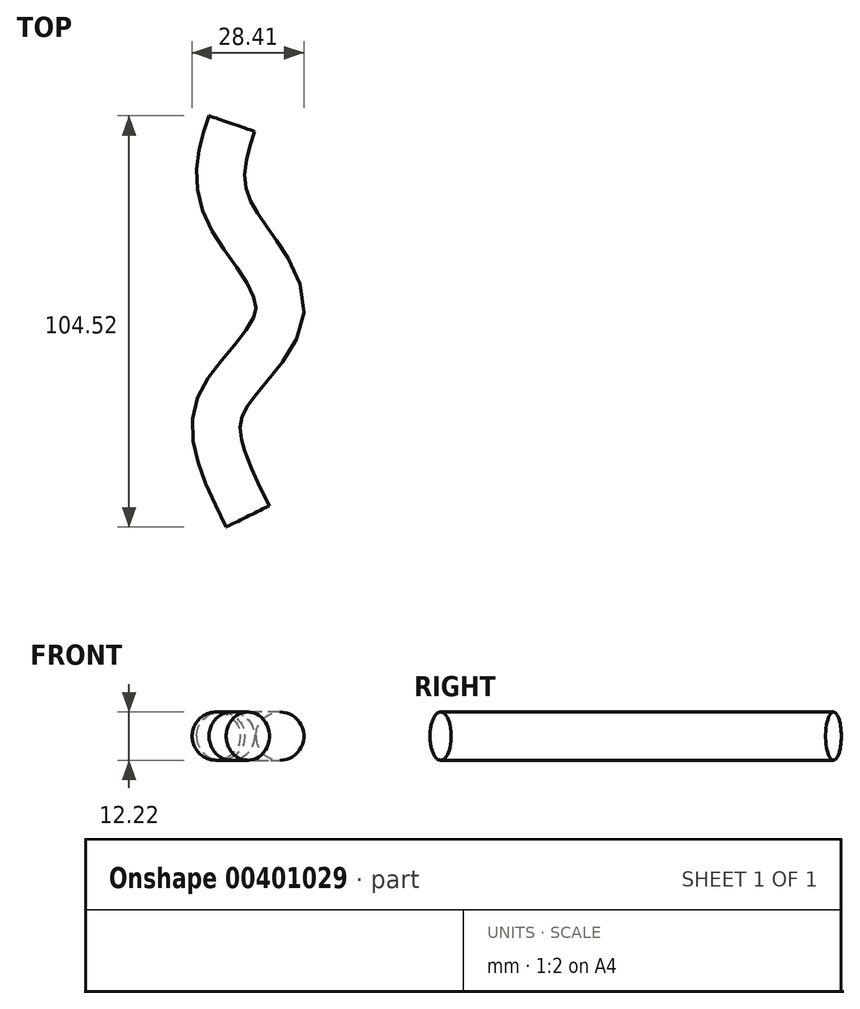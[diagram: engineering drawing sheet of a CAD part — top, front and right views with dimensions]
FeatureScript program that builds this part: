
annotation { "Feature Type Name" : "Feature", "Feature Type Description" : "" }
export const myFeature = defineFeature(function(context is Context, id is Id, definition is map)
    precondition{}
    {
        {
            var Q0;
            Q0=qCreatedBy(makeId("Top.planeOp"),FACE);
            var sketch = newSketch(context, id + "F0", { "sketchPlane" : qUnion([Q0])});
            skFitSpline(sketch, "E0", {"points": [v(-116.4, -34.07) * mm, v(-123.38, -4.26) * mm, v(-108.44, 19.22) * mm, v(-121.97, 45.2) * mm, v(-120.56, 67.16) * mm], "startDerivative": vector(-65.58, 132.57) * mm, "endDerivative": vector(30.7, 88.75) * mm});
            skSolve(sketch);
        }
        {
            var Q0;
            Q0=sQuery(id+"F0.wireOp",EDGE,"E0");
            var Q1;
            Q1=sQuery(id+"F0.wireOp",VERTEX,"E0.start");
            cPlane(context, id + "F1", {"entities" : qUnion([Q0, Q1]), "cplaneType" : CPlaneType.CURVE_POINT, "offset" : 25.4 * mm, "width" : 152.4 * mm, "height" : 152.4 * mm});
        }
        {
            var Q0;
            Q0=qCreatedBy(id+"F1.planeOp",FACE);
            var sketch = newSketch(context, id + "F2", { "sketchPlane" : qUnion([Q0])});
            skCircle(sketch, "E1", {"center": v(117.6, -3.46) * mm, "radius": 6.11 * mm});
            skSolve(sketch);
        }
        {
            var Q0;
            Q0=makeQuery(id+"F2.imprint","IMPRINT",FACE,{"disambiguationData":[TD([[makeQuery(id+"F2.imprint","IMPRINT",EDGE,{"derivedFrom":sQuery(id+"F2.wireOp",EDGE,"E1")}),1.0]])]});
            var Q1;
            Q1=sQuery(id+"F0.wireOp",EDGE,"E0");
            sweep(context, id + "F3", {"profiles" : qUnion([Q0]), "path" : qUnion([Q1])});
        }
    });
